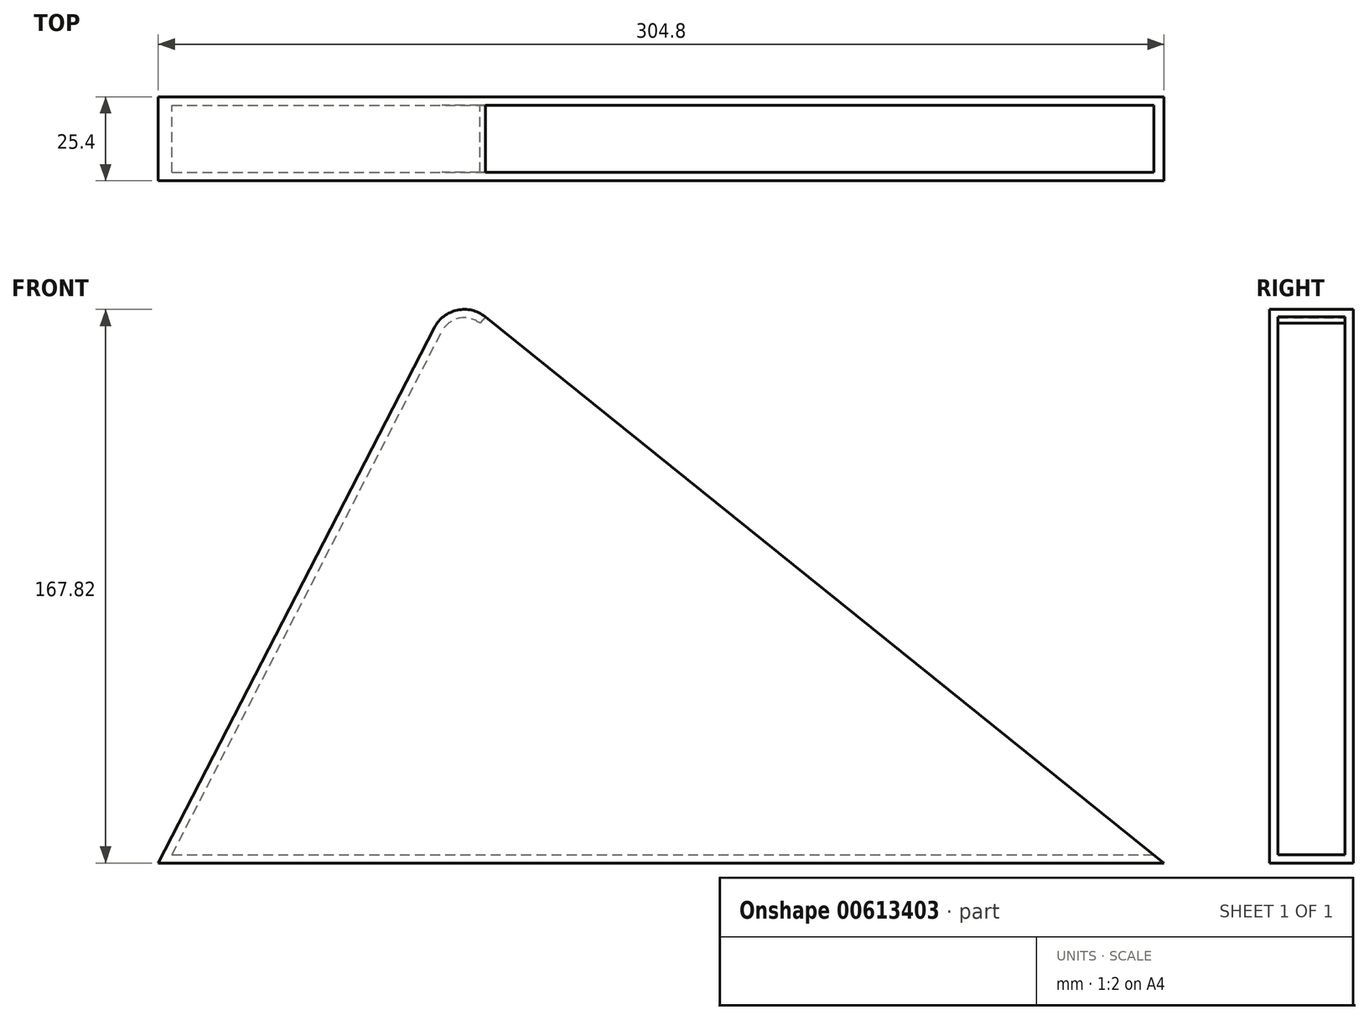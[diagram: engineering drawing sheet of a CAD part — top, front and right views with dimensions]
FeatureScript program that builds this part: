
annotation { "Feature Type Name" : "Feature", "Feature Type Description" : "" }
export const myFeature = defineFeature(function(context is Context, id is Id, definition is map)
    precondition{}
    {
        {
            var Q0;
            Q0=qCreatedBy(makeId("Front.planeOp"),FACE);
            var sketch = newSketch(context, id + "F0", { "sketchPlane" : qUnion([Q0])});
            skLineSegment(sketch, "E0", {"start": v(-143.81, -32.06) * mm, "end": v(160.99, -32.06) * mm});
            skPoint(sketch, "E1.visualSharp", {"position": v(0, 130.73) * mm});
            skLineSegment(sketch, "E2", {"start": v(-143.81, -32.06) * mm, "end": v(-60.15, 130.26) * mm});
            skLineSegment(sketch, "E3", {"start": v(-44.75, 133.52) * mm, "end": v(160.99, -32.06) * mm});
            skPoint(sketch, "E4.visualSharp", {"position": v(-54.45, 141.32) * mm});
            skArc(sketch, "E4.filletArc", {"start": v(-44.75, 133.52) * mm, "mid": v(-53.22, 135.54) * mm, "end": v(-60.15, 130.26) * mm});
            skLineSegment(sketch, "E5", {"start": v(-53.22, 135.54) * mm, "end": v(-53.22, -32.06) * mm});
            skSolve(sketch);
        }
        {
            var Q0;
            Q0=qSketchRegion(id+"F0",true);
            extrude(context, id + "F1", {"entities" : qUnion([Q0]), "depth" : 25.4 * mm, "offsetDistance" : 25.4 * mm});
        }
        {
            var Q0;
            Q0=makeQuery(id+"F1.opExtrude","SWEPT_FACE",FACE,{"disambiguationData":[OSD([sQuery(id+"F0.wireOp",EDGE,"E3")])]});
            shell(context, id + "F2", {"entities" : qUnion([Q0]), "thickness" : 2.54 * mm});
        }
    });
